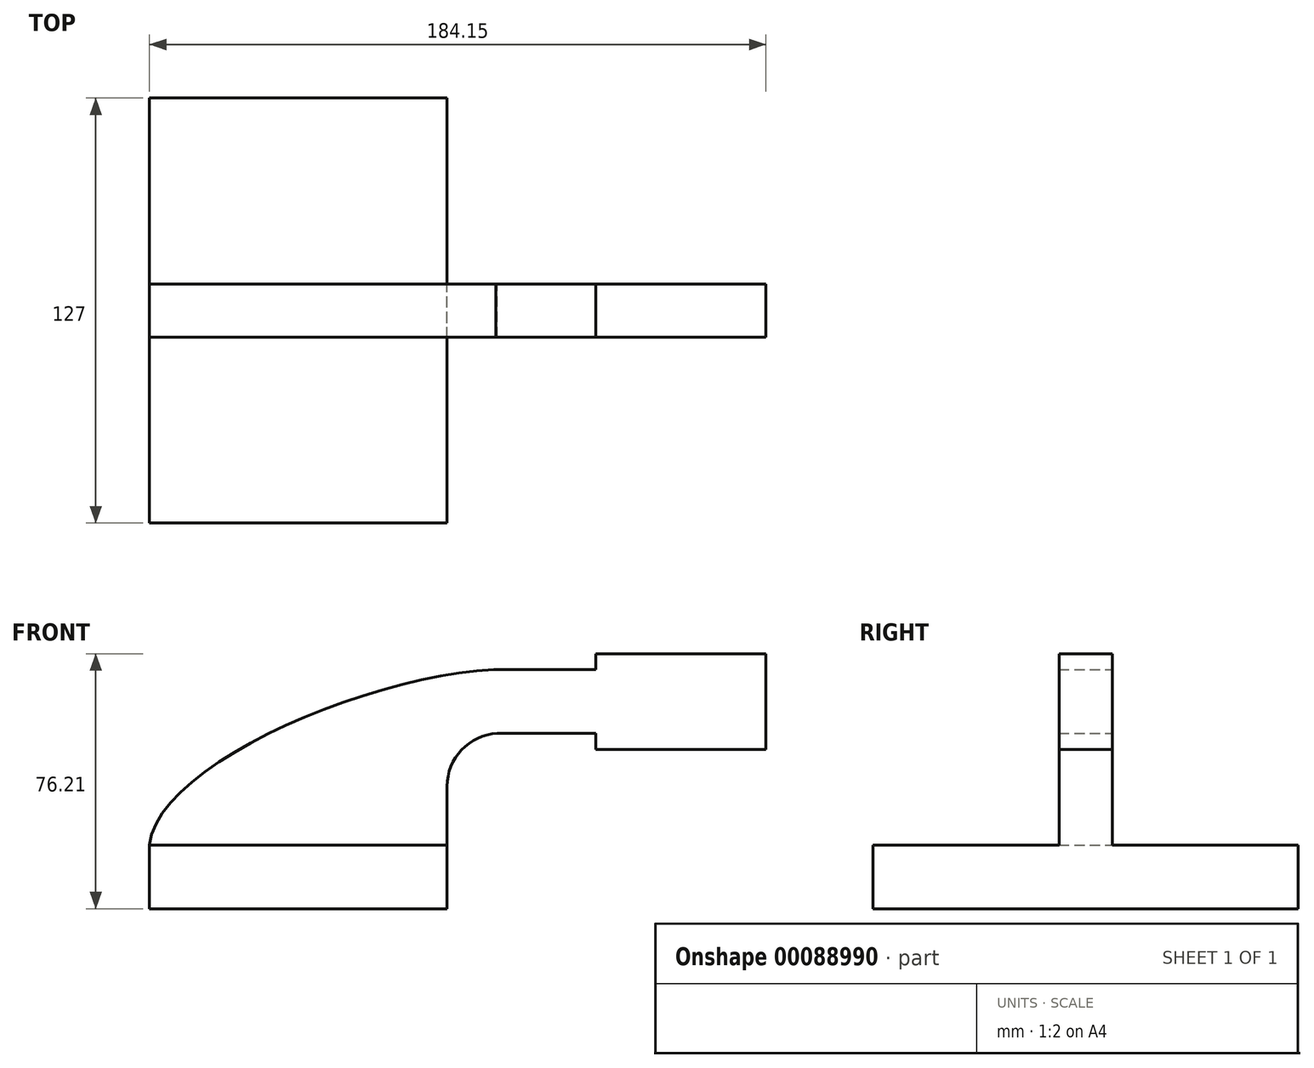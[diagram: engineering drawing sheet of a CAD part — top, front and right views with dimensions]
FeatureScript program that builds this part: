
annotation { "Feature Type Name" : "Feature", "Feature Type Description" : "" }
export const myFeature = defineFeature(function(context is Context, id is Id, definition is map)
    precondition{}
    {
        {
            var Q0;
            Q0=qCreatedBy(makeId("Front.planeOp"),FACE);
            var sketch = newSketch(context, id + "F0", { "sketchPlane" : qUnion([Q0])});
            skLineSegment(sketch, "E0.bottom", {"start": v(-44.45, 9.52) * mm, "end": v(44.45, 9.52) * mm});
            skLineSegment(sketch, "E0.top", {"start": v(-44.45, -9.52) * mm, "end": v(44.45, -9.52) * mm});
            skLineSegment(sketch, "E0.left", {"start": v(-44.45, 9.52) * mm, "end": v(-44.45, -9.52) * mm});
            skLineSegment(sketch, "E0.right", {"start": v(44.45, 9.52) * mm, "end": v(44.45, -9.52) * mm});
            skPoint(sketch, "E0.middle", {"position": v(0, 0) * mm});
            skLineSegment(sketch, "E1.bottom", {"start": v(139.7, 66.68) * mm, "end": v(88.9, 66.68) * mm});
            skLineSegment(sketch, "E1.top", {"start": v(139.7, 38.1) * mm, "end": v(88.9, 38.1) * mm});
            skLineSegment(sketch, "E1.left", {"start": v(139.7, 66.68) * mm, "end": v(139.7, 38.1) * mm});
            skLineSegment(sketch, "E1.right", {"start": v(88.9, 66.68) * mm, "end": v(88.9, 38.1) * mm});
            skPoint(sketch, "E1.middle", {"position": v(114.3, 52.39) * mm});
            skLineSegment(sketch, "E2", {"start": v(114.3, 52.39) * mm, "end": v(114.3, 81.7) * mm});
            skLineSegment(sketch, "E3", {"start": v(114.3, 52.39) * mm, "end": v(114.3, 25.7) * mm});
            skPoint(sketch, "E3.endSnap0", {"position": v(114.3, 38.1) * mm});
            skLineSegment(sketch, "E4", {"start": v(44.45, 9.52) * mm, "end": v(44.45, 27.02) * mm});
            skArc(sketch, "E5", {"start": v(44.45, 27.02) * mm, "mid": v(48.8, 37.93) * mm, "end": v(59.45, 42.88) * mm});
            skLineSegment(sketch, "E6", {"start": v(59.45, 42.88) * mm, "end": v(114.3, 42.88) * mm});
            skLineSegment(sketch, "E7.0", {"start": v(59.02, 61.93) * mm, "end": v(114.3, 61.93) * mm});
            skArc(sketch, "E7.1", {"start": v(25.4, 27.02) * mm, "mid": v(35.17, 51.25) * mm, "end": v(59.02, 61.93) * mm});
            skLineSegment(sketch, "E7.2", {"start": v(25.4, 9.52) * mm, "end": v(25.4, 27.02) * mm});
            skFitSpline(sketch, "E8", {"points": [v(-44.45, 9.52) * mm, v(59.02, 61.93) * mm], "startDerivative": vector(7.38, 72.24) * mm, "endDerivative": vector(113.94, 4.87) * mm});
            skSolve(sketch);
        }
        {
            var Q0;
            Q0=makeQuery(id+"F0.imprint","IMPRINT",FACE,{"disambiguationData":[TD([[makeQuery(id+"F0.imprint","IMPRINT",EDGE,{"derivedFrom":sQuery(id+"F0.wireOp",EDGE,"E0.top")}),1.0]])]});
            extrude(context, id + "F1", {"entities" : qUnion([Q0]), "endBound" : BoundingType.SYMMETRIC, "depth" : 127 * mm});
        }
        {
            var Q0;
            {var subQ3=sQuery(id+"F0.wireOp",EDGE,"E7.2");Q0=makeQuery(id+"F0.imprint","IMPRINT",FACE,{"disambiguationData":[TD([[makeQuery(id+"F0.imprint","IMPRINT",EDGE,{"derivedFrom":subQ3}),1.0]])]});}
            var Q1;
            {var subQ4=sQuery(id+"F0.wireOp",EDGE,"E1.left");Q1=makeQuery(id+"F0.imprint","IMPRINT",FACE,{"disambiguationData":[TD([[makeQuery(id+"F0.imprint","IMPRINT",EDGE,{"derivedFrom":subQ4}),-1.0]])]});}
            var Q2;
            {var subQ3=sQuery(id+"F0.wireOp",EDGE,"E1.right");var subQ7=sQuery(id+"F0.wireOp",EDGE,"E7.0");var subQ9=makeQuery(id+"F0.imprint","INTERSECT",VERTEX,{"derivedFrom":[subQ3,subQ7]});Q2=makeQuery(id+"F0.imprint","IMPRINT",FACE,{"disambiguationData":[TD([[makeQuery(id+"F0.imprint","IMPRINT",EDGE,{"disambiguationData":[TD([[subQ9,-1.0]])],"derivedFrom":subQ3}),1.0]])]});}
            var Q3;
            {var subQ0=sQuery(id+"F0.wireOp",EDGE,"E1.right");var subQ1=sQuery(id+"F0.wireOp",EDGE,"E1.bottom");var subQ2=makeQuery(id+"F0.imprint","INTERSECT",VERTEX,{"derivedFrom":[subQ1,subQ0]});Q3=makeQuery(id+"F0.imprint","IMPRINT",FACE,{"disambiguationData":[TD([[makeQuery(id+"F0.imprint","IMPRINT",EDGE,{"disambiguationData":[TD([[subQ2,1.0]])],"derivedFrom":subQ1}),1.0]])]});}
            var Q4;
            {var subQ0=sQuery(id+"F0.wireOp",EDGE,"E1.right");var subQ1=sQuery(id+"F0.wireOp",EDGE,"E1.top");var subQ2=makeQuery(id+"F0.imprint","INTERSECT",VERTEX,{"derivedFrom":[subQ1,subQ0]});Q4=makeQuery(id+"F0.imprint","IMPRINT",FACE,{"disambiguationData":[TD([[makeQuery(id+"F0.imprint","IMPRINT",EDGE,{"disambiguationData":[TD([[subQ2,1.0]])],"derivedFrom":subQ1}),-1.0]])]});}
            var Q5;
            {var subQ7=sQuery(id+"F0.wireOp",EDGE,"E4");Q5=makeQuery(id+"F0.imprint","IMPRINT",FACE,{"disambiguationData":[TD([[makeQuery(id+"F0.imprint","IMPRINT",EDGE,{"derivedFrom":subQ7}),1.0]])]});}
            extrude(context, id + "F2", {"entities" : qUnion([Q0, Q1, Q2, Q3, Q4, Q5]), "operationType" : NewBodyOperationType.ADD, "endBound" : BoundingType.SYMMETRIC, "depth" : 15.88 * mm});
        }
    });
